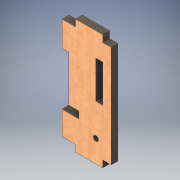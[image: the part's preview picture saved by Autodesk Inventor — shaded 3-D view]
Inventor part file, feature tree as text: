
AUTODESK INVENTOR PART (.ipt)
format: ipt  version: 2019 (Build 230136000, 136)  size: 163,328 bytes
history: native  units: mm
features: extrude x3, sketch x3, other x1
ambient origin geometry x8: Origin, YZ Plane, XZ Plane, XY Plane, X Axis, Y Axis, Z Axis, Center Point
bodies: Body1 (feature_tree)
feature tree (7):
  other  "Твердое тело1"
  extrude  "Выдавливание1"  Depth=16.0mm
  extrude  "Выдавливание2"  Depth=8.0mm
  extrude  "Выдавливание3"  Depth=4.0mm TaperAngle=0.0deg
  sketch  "Эскиз1"
  sketch  "Эскиз2"
  sketch  "Эскиз3"
